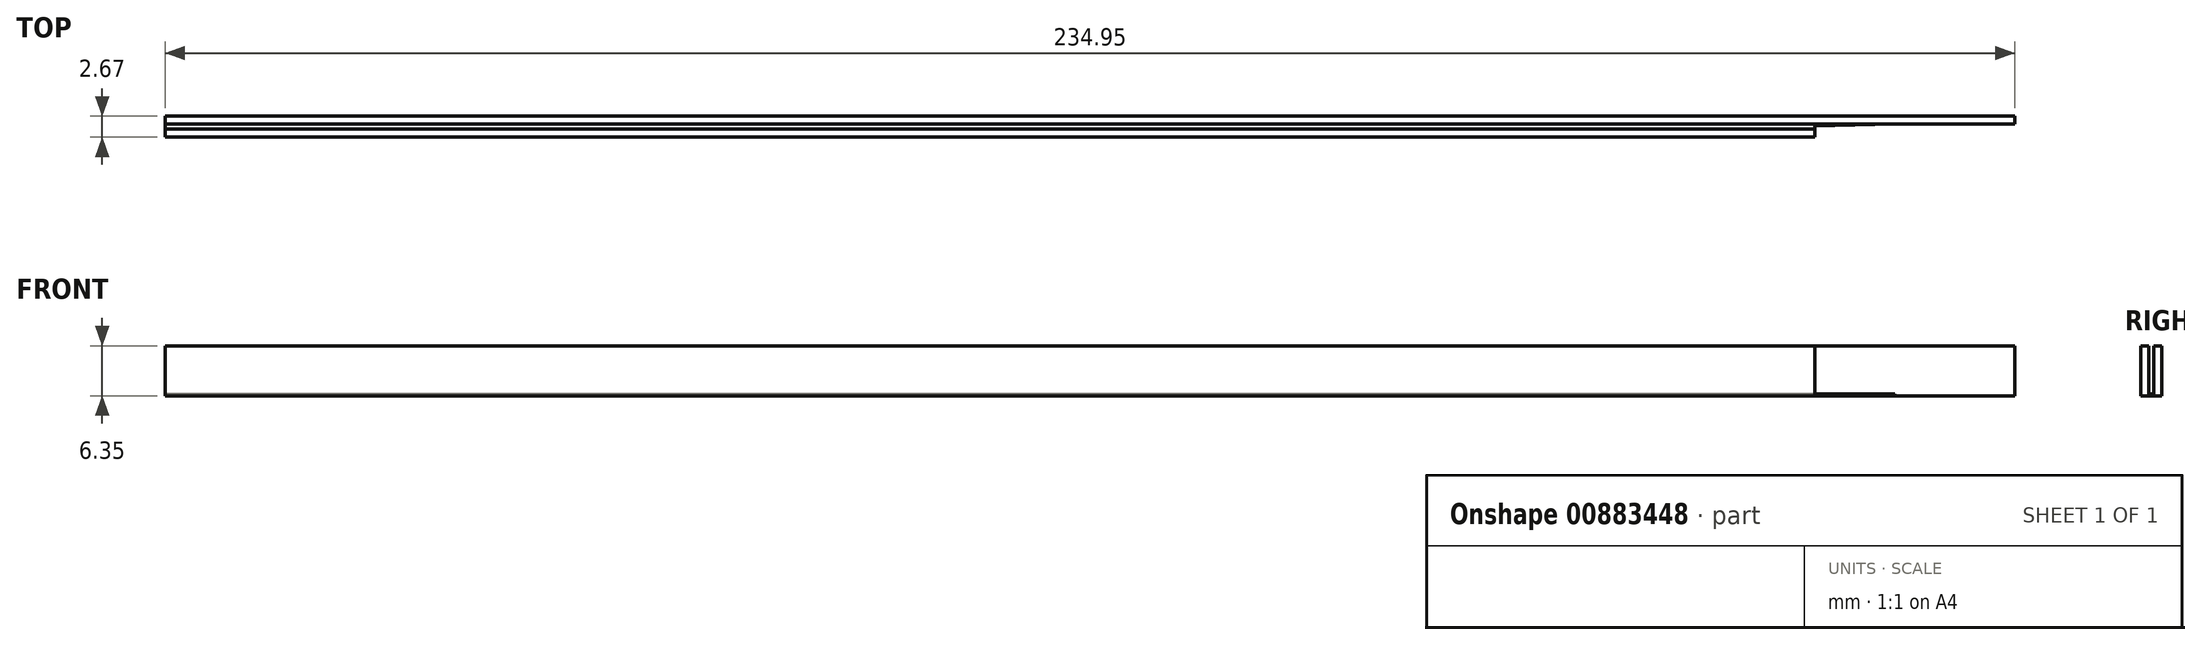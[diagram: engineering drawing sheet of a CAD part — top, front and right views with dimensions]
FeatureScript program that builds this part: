
annotation { "Feature Type Name" : "Feature", "Feature Type Description" : "" }
export const myFeature = defineFeature(function(context is Context, id is Id, definition is map)
    precondition{}
    {
        {
            var Q0;
            Q0=qCreatedBy(makeId("Right.planeOp"),FACE);
            var sketch = newSketch(context, id + "F0", { "sketchPlane" : qUnion([Q0])});
            skLineSegment(sketch, "E0.bottom", {"start": v(0, 0) * mm, "end": v(-2.67, 0) * mm});
            skLineSegment(sketch, "E0.top", {"start": v(0, 6.35) * mm, "end": v(-1.02, 6.35) * mm});
            skLineSegment(sketch, "E0.left", {"start": v(0, 0) * mm, "end": v(0, 6.35) * mm});
            skLineSegment(sketch, "E0.right", {"start": v(-2.67, 0) * mm, "end": v(-2.67, 6.35) * mm});
            skLineSegment(sketch, "E1.top", {"start": v(-1.65, 0.25) * mm, "end": v(-1.02, 0.25) * mm});
            skLineSegment(sketch, "E1.left", {"start": v(-1.65, 6.35) * mm, "end": v(-1.65, 0.25) * mm});
            skLineSegment(sketch, "E1.right", {"start": v(-1.02, 6.35) * mm, "end": v(-1.02, 0.25) * mm});
            skLineSegment(sketch, "E2.trimOffspring", {"start": v(-1.65, 6.35) * mm, "end": v(-2.67, 6.35) * mm});
            skSolve(sketch);
        }
        {
            var Q0;
            Q0 = qSketchRegion(id + "F0", true);
            extrude(context, id + "F1", {"entities" : qUnion([Q0]), "depth" : 234.95 * mm, "offsetDistance" : 25.4 * mm});
        }
        {
            var Q0;
            Q0=makeQuery(id+"F1.opExtrude","SWEPT_FACE",FACE,{"disambiguationData":[OSD([sQuery(id+"F0.wireOp",EDGE,"E0.bottom")])]});
            var sketch = newSketch(context, id + "F2", { "sketchPlane" : qUnion([Q0])});
            skLineSegment(sketch, "E3.bottom", {"start": v(240.68, 9.77) * mm, "end": v(209.55, 9.77) * mm});
            skLineSegment(sketch, "E3.left", {"start": v(240.68, 9.77) * mm, "end": v(240.68, 1.02) * mm});
            skLineSegment(sketch, "E3.right", {"start": v(209.55, 9.77) * mm, "end": v(209.55, 1.27) * mm});
            skLineSegment(sketch, "E4.0", {"start": v(209.54, 1.27) * mm, "end": v(219.7, 1.02) * mm});
            skLineSegment(sketch, "E5", {"start": v(240.68, 1.02) * mm, "end": v(219.7, 1.02) * mm});
            skSolve(sketch);
        }
        {
            var Q0;
            Q0 = qSketchRegion(id + "F2", true);
            extrude(context, id + "F3", {"entities" : qUnion([Q0]), "operationType" : NewBodyOperationType.REMOVE, "oppositeDirection" : true, "depth" : 25.4 * mm, "offsetDistance" : 25.4 * mm});
        }
    });
